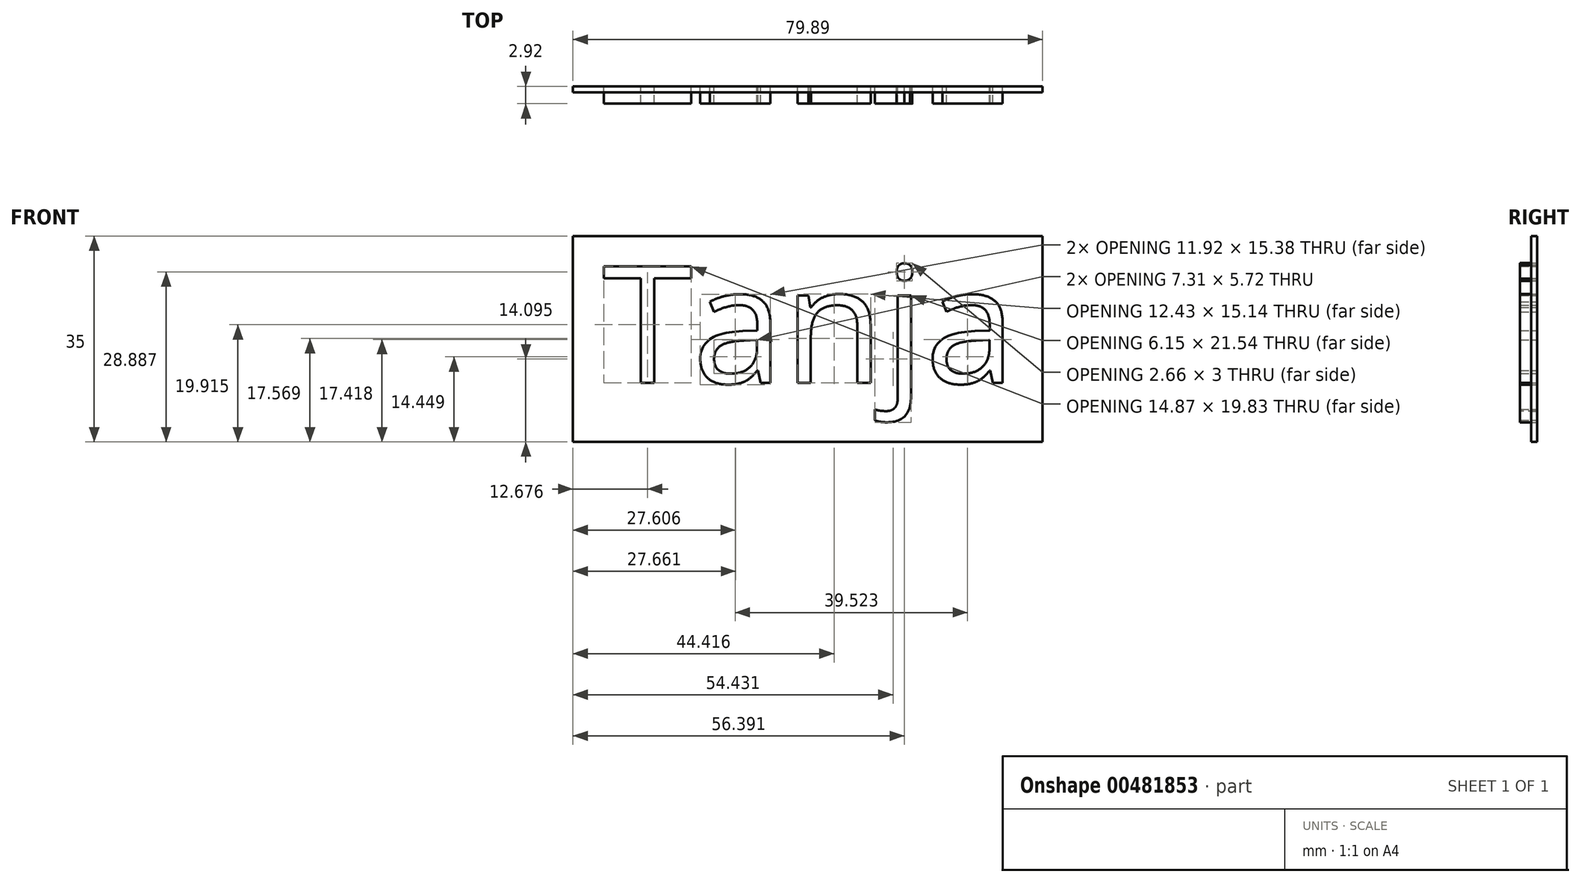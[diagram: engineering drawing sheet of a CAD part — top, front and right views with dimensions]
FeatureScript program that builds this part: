
annotation { "Feature Type Name" : "Feature", "Feature Type Description" : "" }
export const myFeature = defineFeature(function(context is Context, id is Id, definition is map)
    precondition{}
    {
        {
            var Q0;
            Q0=qCreatedBy(makeId("Front.planeOp"),FACE);
            var sketch = newSketch(context, id + "F0", { "sketchPlane" : qUnion([Q0])});
            skText(sketch, "E0", { "text": "Tanja", "fontName": "OpenSans-Regular.ttf"});
            skLineSegment(sketch, "E1.bottom", {"start": v(-5, -10) * mm, "end": v(74.9, -10) * mm});
            skLineSegment(sketch, "E1.top", {"start": v(-5, 25) * mm, "end": v(74.9, 25) * mm});
            skLineSegment(sketch, "E1.left", {"start": v(-5, -10) * mm, "end": v(-5, 25) * mm});
            skLineSegment(sketch, "E1.right", {"start": v(74.9, -10) * mm, "end": v(74.9, 25) * mm});
            const initialGuessF0  = {"E0": [0, 0, 1, 0, 0.02]};
            skSetInitialGuess(sketch, initialGuessF0);
            skSolve(sketch);
        }
        {
            var Q0;
            Q0=makeQuery(id+"F0.imprint","IMPRINT",FACE,{"disambiguationData":[TD([[makeQuery(id+"F0.imprint","IMPRINT",EDGE,{"derivedFrom":sQuery(id+"F0.wireOp",EDGE,"E0.sketch_text.stroke-0")}),-1.0]])]});
            var Q1;
            Q1=makeQuery(id+"F0.imprint","IMPRINT",FACE,{"disambiguationData":[TD([[makeQuery(id+"F0.imprint","IMPRINT",EDGE,{"derivedFrom":sQuery(id+"F0.wireOp",EDGE,"E0.sketch_text.stroke-25")}),-1.0]])]});
            var Q2;
            Q2=makeQuery(id+"F0.imprint","IMPRINT",FACE,{"disambiguationData":[TD([[makeQuery(id+"F0.imprint","IMPRINT",EDGE,{"derivedFrom":sQuery(id+"F0.wireOp",EDGE,"E0.sketch_text.stroke-44")}),-1.0]])]});
            var Q3;
            Q3=makeQuery(id+"F0.imprint","IMPRINT",FACE,{"disambiguationData":[TD([[makeQuery(id+"F0.imprint","IMPRINT",EDGE,{"derivedFrom":sQuery(id+"F0.wireOp",EDGE,"E0.sketch_text.stroke-71")}),-1.0]])]});
            var Q4;
            Q4=makeQuery(id+"F0.imprint","IMPRINT",FACE,{"disambiguationData":[TD([[makeQuery(id+"F0.imprint","IMPRINT",EDGE,{"derivedFrom":sQuery(id+"F0.wireOp",EDGE,"E0.sketch_text.stroke-88")}),-1.0]])]});
            var Q5;
            Q5=makeQuery(id+"F0.imprint","IMPRINT",FACE,{"disambiguationData":[TD([[makeQuery(id+"F0.imprint","IMPRINT",EDGE,{"derivedFrom":sQuery(id+"F0.wireOp",EDGE,"E0.sketch_text.stroke-52")}),-1.0]])]});
            var Q6;
            Q6=makeQuery(id+"F0.imprint","IMPRINT",FACE,{"disambiguationData":[TD([[makeQuery(id+"F0.imprint","IMPRINT",EDGE,{"derivedFrom":sQuery(id+"F0.wireOp",EDGE,"E0.sketch_text.stroke-61")}),-1.0]])]});
            extrude(context, id + "F1", {"entities" : qUnion([Q0, Q1, Q2, Q3, Q4, Q5, Q6]), "depth" : 2.92 * mm});
        }
        {
            var Q0;
            Q0=makeQuery(id+"F0.imprint","IMPRINT",FACE,{"disambiguationData":[TD([[makeQuery(id+"F0.imprint","IMPRINT",EDGE,{"derivedFrom":sQuery(id+"F0.wireOp",EDGE,"E0.sketch_text.stroke-88")}),1.0]])]});
            var Q1;
            Q1=makeQuery(id+"F0.imprint","IMPRINT",FACE,{"disambiguationData":[TD([[makeQuery(id+"F0.imprint","IMPRINT",EDGE,{"derivedFrom":sQuery(id+"F0.wireOp",EDGE,"E0.sketch_text.stroke-0")}),1.0]])]});
            var Q2;
            Q2=makeQuery(id+"F0.imprint","IMPRINT",FACE,{"disambiguationData":[TD([[makeQuery(id+"F0.imprint","IMPRINT",EDGE,{"derivedFrom":sQuery(id+"F0.wireOp",EDGE,"E0.sketch_text.stroke-27")}),1.0]])]});
            extrude(context, id + "F2", {"entities" : qUnion([Q0, Q1, Q2]), "depth" : 1 * mm});
        }
    });
